# Revit family: Bolt-Assembly-Steel & Tube-ISO Metric
name_source: partatom
category: Structural Connections
revit_build: Autodesk Revit 2016 (Build: 20161004_0715(x64)
units: mm (PartAtom-declared; Revit-internal decimal feet)

## family parameters
Cut with Voids When Loaded = No
Enable cutting in views = Yes
Host = Face
Material for Model Behavior = Steel
OmniClass Number = 23.20.40.11.14.27
OmniClass Title = Bolts and Nuts
Shared = Yes

## types (12) — shared parameters
CBICode = 3411
CBIDescription = Structural steelwork
Description = ISO Metric Precision Hexagon Bolt in accordance with BS 3692:2001
Manufacturer = Steel & Tube
ManufacturerName = Steel & Tube
ManufacturerURL = http://www.steelandtube.co.nz
Material_ANZRS = Metal-Steel-450MPa
ModifiedIssue_ANZRS = 20160526 $
SpecificationDescription = Steel & Tube Purlins & Girts
SpecificationReference = 3411ST
Type Comments = Bolt Assembly
URL = http://www.steelandtube.co.nz
Uniclass2015Code = Pr_20_76_51_21
Uniclass2015Title = Cold-formed galvanized steel sections
Uniclass2015Version = 2015
zero-valued in all types: Default Elevation

## per-type parameters (varying)
| type | Arc Height | Bolt Diameter | Bolt Head | Centreline Size | Cove | Height_ANZRS | Nut | Nut Cross Section | Nut Size | Washer Diameter | Width_ANZRS |
| M3 | 0.413 mm | 3 mm  [stored 0.00984252 ft] | 2.125 mm | 11 mm | 4.5 mm | 6.351 mm | 2.4 mm  [stored 0.00787402 ft] | 6.351 mm | 5.5 mm  [stored 0.0180446 ft] | 7 mm  [stored 0.0229659 ft] | 6.351 mm |
| M4 | 0.551 mm | 4 mm  [stored 0.0131234 ft] | 2.925 mm  [stored 0.00959646 ft] | 14 mm | 6 mm  [stored 0.019685 ft] | 8.083 mm | 3.2 mm  [stored 0.0104987 ft] | 8.083 mm | 7 mm  [stored 0.0229659 ft] | 9 mm  [stored 0.0295276 ft] | 8.083 mm |
| M5 | 0.688 mm | 5 mm  [stored 0.0164042 ft] | 3.65 mm  [stored 0.0119751 ft] | 16 mm | 7.5 mm  [stored 0.0246063 ft] | 9.238 mm | 4 mm  [stored 0.0131234 ft] | 9.238 mm | 8 mm  [stored 0.0262467 ft] | 10 mm  [stored 0.0328084 ft] | 9.238 mm |
| M6 | 0.826 mm | 6 mm  [stored 0.019685 ft] | 4.15 mm  [stored 0.0136155 ft] | 20 mm | 9 mm  [stored 0.0295276 ft] | 11.547 mm | 5 mm  [stored 0.0164042 ft] | 11.547 mm | 10 mm  [stored 0.0328084 ft] | 12.5 mm | 11.547 mm |
| M8 | 1.101 mm | 8 mm  [stored 0.0262467 ft] | 5.65 mm  [stored 0.0185367 ft] | 26 mm | 12 mm | 15.011 mm | 6.5 mm | 15.011 mm | 13 mm | 17 mm | 15.011 mm |
| M10 | 1.376 mm | 10 mm  [stored 0.0328084 ft] | 7.18 mm  [stored 0.0235564 ft] | 34 mm | 15 mm | 19.63 mm | 8 mm  [stored 0.0262467 ft] | 19.63 mm | 17 mm | 21 mm | 19.63 mm |
| M12 | 1.652 mm | 12 mm | 8.18 mm  [stored 0.0268373 ft] | 38 mm | 18 mm | 21.939 mm | 10 mm  [stored 0.0328084 ft] | 21.939 mm | 19 mm | 24 mm | 21.939 mm |
| M16 | 2.202 mm | 16 mm | 10.18 mm  [stored 0.0333989 ft] | 48 mm | 24 mm | 27.713 mm | 13 mm | 27.713 mm | 24 mm | 30 mm | 27.713 mm |
| M20 | 2.753 mm | 20 mm | 13.215 mm | 60 mm | 30 mm | 34.641 mm | 16 mm | 34.641 mm | 30 mm | 37 mm | 34.641 mm |
| M24 | 3.303 mm | 24 mm | 15.215 mm | 72 mm | 36 mm | 41.569 mm | 19 mm | 41.569 mm | 36 mm | 44 mm | 41.569 mm |
| M30 | 4.129 mm | 30 mm | 19.26 mm | 92 mm | 45 mm | 53.116 mm | 24 mm | 53.116 mm | 46 mm | 56 mm | 53.116 mm |
| M36 | 4.955 mm | 36 mm | 23.26 mm | 110 mm | 54 mm | 63.509 mm | 29 mm | 63.509 mm | 55 mm | 66 mm | 63.509 mm |

note: column(s) folded — value = type name in every type: Model

note: [stored X ft] marks values corroborated as IEEE doubles in the binary element streams (Revit-internal decimal feet)

## geometry (parser evidence)
native form markers: Sweep x2
no freeform markers — native parametric forms only
